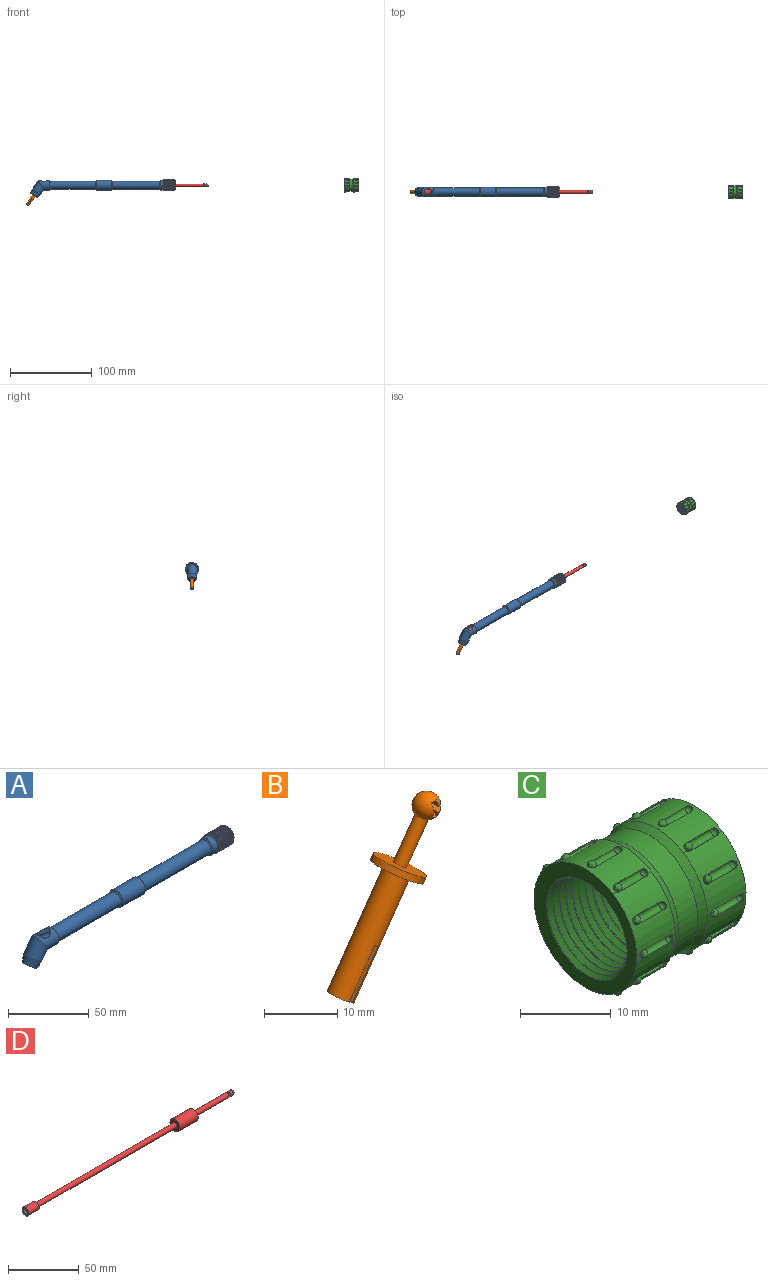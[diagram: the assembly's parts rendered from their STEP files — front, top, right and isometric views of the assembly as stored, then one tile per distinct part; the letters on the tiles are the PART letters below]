
ASSEMBLY  parts=4 mates=3
PART A: 38 faces, bbox 177.7x13x25.7 mm
  f0: bspline ~15.48x15.01mm, area 394.4mm2, adj f1,f2,f4,f5,f6,f7,f8,f9
  f1: bspline ~15.01x14.64mm, area 380.3mm2, adj f0,f3,f4,f5,f6,f7,f8,f9
  f2: cylinder r=6mm len=12mm, axis (-1,0,0), area 132.3mm2, adj f0,f17,f31,f37
  f3: cylinder r=6mm len=1.9mm, axis (-1,0,0), area 0mm2, adj f1,f4,f36
  f4: cylinder r=6mm len=12mm, axis (-1,0,0), area 1.9mm2, adj f0,f1,f3,f5
  f5: cylinder r=6mm len=12mm, axis (-1,0,0), area 1.9mm2, adj f0,f1,f4,f6
  f6: cylinder r=6mm len=12mm, axis (-1,0,0), area 1.9mm2, adj f0,f1,f5,f7
  f7: cylinder r=6mm len=12mm, axis (-1,0,0), area 1.9mm2, adj f0,f1,f6,f8
  f8: cylinder r=6mm len=12mm, axis (-1,0,0), area 1.9mm2, adj f0,f1,f7,f9
  f9: cylinder r=6mm len=12mm, axis (-1,0,0), area 1.9mm2, adj f0,f1,f8,f10
  f10: cylinder r=6mm len=12mm, axis (-1,0,0), area 1.9mm2, adj f0,f1,f9,f11
  f11: cylinder r=6mm len=12mm, axis (-1,0,0), area 1.9mm2, adj f0,f1,f10,f12
  f12: cylinder r=6mm len=12mm, axis (-1,0,0), area 1.9mm2, adj f0,f1,f11,f13
  f13: cylinder r=6mm len=12mm, axis (-1,0,0), area 1.9mm2, adj f0,f1,f12,f14
  f14: cylinder r=6mm len=12mm, axis (-1,0,0), area 1.9mm2, adj f0,f1,f13,f15
  f15: cylinder r=6mm len=12mm, axis (-1,0,0), area 1.9mm2, adj f0,f1,f14,f16
  f16: cylinder r=6mm len=12mm, axis (-1,0,0), area 1.9mm2, adj f0,f1,f15,f17
  f17: cylinder r=6mm len=12mm, axis (-1,0,0), area 1.9mm2, adj f0,f1,f2,f16
  f18: cylinder r=4mm len=21.07mm, axis (-0.57,0,-0.82), area 373.9mm2, adj f21,f28,f30
  f19: cylinder r=5mm len=54.5mm, axis (-1,0,0), area 1712.2mm2, adj f33,f34
  f20: cylinder r=5mm len=57.5mm, axis (-1,0,0), area 1806.4mm2, adj f31,f32
  f21: cylinder r=4mm len=147mm, axis (-1,0,0), area 3633mm2, adj f18,f23
  f22: plane 10x8.19mm, normal (-0.57,0,-0.82), area 66mm2, adj f29,f35
  f23: plane 10x10mm, normal (1,0,0), area 28.3mm2, adj f21,f24
  f24: cylinder r=5mm len=18mm, axis (-1,0,0), area 565.5mm2, adj f23,f25
  f25: plane 10.02x10.02mm, normal (1,0,0), area 0.3mm2, adj f24,f36
  f26: cylinder r=6mm len=19mm, axis (-1,0,0), area 716.3mm2, adj f32,f33
  f27: cylinder r=6mm len=17.63mm, axis (-0.57,0,-0.82), area 494.7mm2, adj f28,f35
  f28: cylinder r=6mm len=14.13mm, axis (-1,0,0), area 349.2mm2, adj f18,f27,f34
  f29: cylinder r=2mm len=6.39mm, axis (0.57,0,0.82), area 62.8mm2, adj f22,f30
  f30: plane 8x6.55mm, normal (0.57,0,0.82), area 37.7mm2, adj f18,f29
  f31: cone r=5mm half-angle=45deg, axis (1,0,0), area 48.9mm2, adj f2,f20
  f32: cone r=6mm half-angle=45deg, axis (-1,0,0), area 48.9mm2, adj f20,f26
  f33: cone r=6mm half-angle=45deg, axis (1,0,0), area 48.9mm2, adj f19,f26
  f34: cone r=7mm half-angle=45deg, axis (-1,0,0), area 48.9mm2, adj f19,f28
  f35: cone r=6mm half-angle=11.3deg, axis (0.57,0,0.82), area 176.2mm2, adj f22,f27
  f36: cone r=6mm half-angle=45deg, axis (-1,0,0), area 61.4mm2, adj f0,f1,f3,f25
  f37: plane 0.95x0.5mm, normal (0,0,1), area 0.2mm2, adj f0,f1,f2
PART B: 25 faces, bbox 20.3x8x26.9 mm
  f0: sphere r=2mm, area 35.4mm2, adj f2,f4,f6,f15,f16,f17,f18,f19
  f1: cylinder r=0.5mm len=1mm, axis (0,1,0), area 0.5mm2, adj f2,f15,f22
  f2: plane 3.74x1.94mm, normal (0,0,-1), area 4.5mm2, adj f0,f1,f15,f17,f21,f22
  f3: cylinder r=0.5mm len=1mm, axis (0,1,0), area 0.5mm2, adj f4,f18,f23
  f4: plane 3.74x1.94mm, normal (0,0,1), area 4.5mm2, adj f0,f3,f18,f19,f23,f24
  f5: plane 3.91x1.3mm, normal (-0.57,0,-0.82), area 4.6mm2, adj f10,f14
  f6: cylinder r=1mm len=7.1mm, axis (0.57,0,0.82), area 45.7mm2, adj f0,f7
  f7: plane 8x6.55mm, normal (0.57,0,0.82), area 47.1mm2, adj f6,f8
  f8: cylinder r=4mm len=8mm, axis (0.57,0,0.82), area 25.1mm2, adj f7,f9
  f9: plane 8x6.55mm, normal (-0.57,0,-0.82), area 37.7mm2, adj f8,f10
  f10: cylinder r=2mm len=17.86mm, axis (0.57,0,0.82), area 224.7mm2, adj f5,f9,f11,f12,f13,f14
  f11: plane 3.92x1.31mm, normal (-0.57,0,-0.82), area 4.7mm2, adj f10,f13
  f12: plane 4x0.67mm, normal (-0.57,0,-0.82), area 3.2mm2, adj f10,f13,f14
  f13: plane 7.04x4.93mm, normal (0.82,0,-0.57), area 33.7mm2, adj f10,f11,f12
  f14: plane 7.04x4.93mm, normal (-0.82,0,0.57), area 33.6mm2, adj f5,f10,f12
  f15: plane 1.41x1.41mm, normal (0,0.71,-0.71), area 1.3mm2, adj f0,f1,f2,f16,f17
  f16: plane 2.74x1.94mm, normal (1,0,0), area 2.9mm2, adj f0,f15,f18
  f17: plane 1.37x0.87mm, normal (-1,0,0), area 0.6mm2, adj f0,f2,f15
  f18: plane 1.41x1.41mm, normal (0,0.71,0.71), area 1.3mm2, adj f0,f3,f4,f16,f19
  f19: plane 1.37x0.87mm, normal (-1,0,0), area 0.6mm2, adj f0,f4,f18
  f20: plane 2.74x1.94mm, normal (1,0,0), area 2.9mm2, adj f0,f22,f23
  f21: plane 1.37x0.87mm, normal (-1,0,0), area 0.6mm2, adj f0,f2,f22
  f22: plane 1.41x1.41mm, normal (0,-0.71,-0.71), area 1.3mm2, adj f0,f1,f2,f20,f21
  f23: plane 1.41x1.41mm, normal (0,-0.71,0.71), area 1.3mm2, adj f0,f3,f4,f20,f24
  f24: plane 1.37x0.87mm, normal (-1,0,0), area 0.6mm2, adj f0,f4,f23
PART C: 85 faces, bbox 18.1x17.4x17.4 mm
  f0: sphere r=0.5mm, area 2.1mm2, adj f1,f3
  f1: cylinder r=0.5mm len=4mm, axis (1,0,0), area 6.2mm2, adj f0,f2,f3
  f2: sphere r=0.5mm, area 1.1mm2, adj f1,f3
  f3: cylinder r=8mm len=16mm, axis (1,0,0), area 247.6mm2, adj f0,f1,f2,f4,f5,f6,f7,f8
  f4: sphere r=0.5mm, area 1.1mm2, adj f3,f6
  f5: sphere r=0.5mm, area 2.1mm2, adj f3,f6
  f6: cylinder r=0.5mm len=4mm, axis (1,0,0), area 6.2mm2, adj f3,f4,f5
  f7: sphere r=0.5mm, area 1.1mm2, adj f3,f9
  f8: sphere r=0.5mm, area 2.1mm2, adj f3,f9
  f9: cylinder r=0.5mm len=4mm, axis (1,0,0), area 6.2mm2, adj f3,f7,f8
  f10: sphere r=0.5mm, area 1.1mm2, adj f3,f12
  f11: sphere r=0.5mm, area 2.1mm2, adj f3,f12
  f12: cylinder r=0.5mm len=4mm, axis (1,0,0), area 6.2mm2, adj f3,f10,f11
  f13: sphere r=0.5mm, area 1.1mm2, adj f3,f15
  f14: sphere r=0.5mm, area 2.1mm2, adj f3,f15
  f15: cylinder r=0.5mm len=4mm, axis (1,0,0), area 6.2mm2, adj f3,f13,f14
  f16: sphere r=0.5mm, area 1.1mm2, adj f3,f18
  f17: sphere r=0.5mm, area 2.1mm2, adj f3,f18
  f18: cylinder r=0.5mm len=4mm, axis (1,0,0), area 6.2mm2, adj f3,f16,f17
  f19: sphere r=0.5mm, area 1.1mm2, adj f3,f21
  f20: sphere r=0.5mm, area 2.1mm2, adj f3,f21
  f21: cylinder r=0.5mm len=4mm, axis (1,0,0), area 6.2mm2, adj f3,f19,f20
  f22: sphere r=0.5mm, area 1.1mm2, adj f3,f24
  f23: sphere r=0.5mm, area 2.1mm2, adj f3,f24
  f24: cylinder r=0.5mm len=4mm, axis (1,0,0), area 6.2mm2, adj f3,f22,f23
  f25: sphere r=0.5mm, area 1.1mm2, adj f3,f27
  f26: sphere r=0.5mm, area 2.1mm2, adj f3,f27
  f27: cylinder r=0.5mm len=4mm, axis (1,0,0), area 6.2mm2, adj f3,f25,f26
  f28: sphere r=0.5mm, area 1.1mm2, adj f3,f30
  f29: sphere r=0.5mm, area 2.1mm2, adj f3,f30
  f30: cylinder r=0.5mm len=4mm, axis (1,0,0), area 6.2mm2, adj f3,f28,f29
  f31: sphere r=0.5mm, area 1.1mm2, adj f3,f33
  f32: sphere r=0.5mm, area 2.1mm2, adj f3,f33
  f33: cylinder r=0.5mm len=4mm, axis (1,0,0), area 6.2mm2, adj f3,f31,f32
  f34: plane 16x16mm, normal (1,0,0), area 188.5mm2, adj f3,f35
  f35: cylinder r=2mm len=4mm, axis (1,0,0), area 25.1mm2, adj f34,f36
  f36: plane 12x12mm, normal (-1,0,0), area 100.5mm2, adj f35,f37
  f37: cylinder r=6mm len=15mm, axis (1,0,0), area -52mm2, adj f36,f38,f39,f79,f80
  f38: bspline ~15.5x15.01mm, area 409.7mm2, adj f37,f39,f79,f80
  f39: plane 16.45x16.45mm, normal (-1,0,0), area 78.4mm2, adj f37,f38,f40,f79
  f40: cylinder r=8mm len=16mm, axis (1,0,0), area 247.6mm2, adj f39,f41,f42,f43,f44,f45,f46,f47
  f41: sphere r=0.5mm, area 1.1mm2, adj f40,f43
  f42: sphere r=0.5mm, area 2.1mm2, adj f40,f43
  f43: cylinder r=0.5mm len=4mm, axis (1,0,0), area 6.2mm2, adj f40,f41,f42
  f44: sphere r=0.5mm, area 1.1mm2, adj f40,f46
  f45: sphere r=0.5mm, area 2.1mm2, adj f40,f46
  f46: cylinder r=0.5mm len=4mm, axis (1,0,0), area 6.2mm2, adj f40,f44,f45
  f47: sphere r=0.5mm, area 1.1mm2, adj f40,f49
  f48: sphere r=0.5mm, area 2.1mm2, adj f40,f49
  f49: cylinder r=0.5mm len=4mm, axis (1,0,0), area 6.2mm2, adj f40,f47,f48
  f50: sphere r=0.5mm, area 1.1mm2, adj f40,f52
  f51: sphere r=0.5mm, area 2.1mm2, adj f40,f52
  f52: cylinder r=0.5mm len=4mm, axis (1,0,0), area 6.2mm2, adj f40,f50,f51
  f53: sphere r=0.5mm, area 1.1mm2, adj f40,f55
  f54: sphere r=0.5mm, area 2.1mm2, adj f40,f55
  f55: cylinder r=0.5mm len=4mm, axis (1,0,0), area 6.2mm2, adj f40,f53,f54
  f56: sphere r=0.5mm, area 1.1mm2, adj f40,f58
  f57: sphere r=0.5mm, area 2.1mm2, adj f40,f58
  f58: cylinder r=0.5mm len=4mm, axis (1,0,0), area 6.2mm2, adj f40,f56,f57
  f59: sphere r=0.5mm, area 1.1mm2, adj f40,f61
  f60: sphere r=0.5mm, area 2.1mm2, adj f40,f61
  f61: cylinder r=0.5mm len=4mm, axis (1,0,0), area 6.2mm2, adj f40,f59,f60
  f62: sphere r=0.5mm, area 1.1mm2, adj f40,f64
  f63: sphere r=0.5mm, area 2.1mm2, adj f40,f64
  f64: cylinder r=0.5mm len=4mm, axis (1,0,0), area 6.2mm2, adj f40,f62,f63
  f65: sphere r=0.5mm, area 1.1mm2, adj f40,f67
  f66: sphere r=0.5mm, area 2.1mm2, adj f40,f67
  f67: cylinder r=0.5mm len=4mm, axis (1,0,0), area 6.2mm2, adj f40,f65,f66
  f68: sphere r=0.5mm, area 1.1mm2, adj f40,f70
  f69: sphere r=0.5mm, area 2.1mm2, adj f40,f70
  f70: cylinder r=0.5mm len=4mm, axis (1,0,0), area 6.2mm2, adj f40,f68,f69
  f71: sphere r=0.5mm, area 1.1mm2, adj f40,f73
  f72: sphere r=0.5mm, area 2.1mm2, adj f40,f73
  f73: cylinder r=0.5mm len=4mm, axis (1,0,0), area 6.2mm2, adj f40,f71,f72
  f74: cone r=8mm half-angle=26.6deg, axis (-1,0,0), area 54.4mm2, adj f40,f75
  f75: cylinder r=7.5mm len=15mm, axis (1,0,0), area 141.4mm2, adj f74,f82
  f76: sphere r=0.5mm, area 1.1mm2, adj f40,f78
  f77: sphere r=0.5mm, area 2.1mm2, adj f40,f78
  f78: cylinder r=0.5mm len=4mm, axis (1,0,0), area 6.2mm2, adj f40,f76,f77
  f79: bspline ~15.16x15.01mm, area 396.2mm2, adj f37,f38,f39,f80
  f80: plane 0.99x0.5mm, normal (0,0,-1), area 0.2mm2, adj f37,f38,f79
  f81: sphere r=0.5mm, area 1.1mm2, adj f3,f84
  f82: cone r=7.5mm half-angle=26.6deg, axis (1,0,0), area 54.4mm2, adj f3,f75
  f83: sphere r=0.5mm, area 2.1mm2, adj f3,f84
  f84: cylinder r=0.5mm len=4mm, axis (1,0,0), area 6.2mm2, adj f3,f81,f83
PART D: 14 faces, bbox 207x10x10 mm
  f0: cylinder r=2mm len=4mm, axis (1,0,0), area 24.3mm2, adj f1,f12,f13
  f1: sphere r=2mm, area 24.3mm2, adj f0,f13
  f2: sphere r=2mm, area 25.1mm2, adj f3
  f3: cylinder r=2mm len=4mm, axis (1,0,0), area 31.8mm2, adj f2,f4
  f4: torus R=2.12mm, axis (1,0,0), area 21.1mm2, adj f3,f5
  f5: cylinder r=2mm len=33.99mm, axis (1,0,0), area 427.1mm2, adj f4,f6
  f6: plane 10x10mm, normal (1,0,0), area 66mm2, adj f5,f7
  f7: cylinder r=5mm len=18mm, axis (1,0,0), area 565.5mm2, adj f6,f8
  f8: plane 10x10mm, normal (-1,0,0), area 66mm2, adj f7,f9
  f9: cylinder r=2mm len=139mm, axis (1,0,0), area 1746.7mm2, adj f8,f10
  f10: plane 7x7mm, normal (1,0,0), area 25.9mm2, adj f9,f11
  f11: cylinder r=3.5mm len=10mm, axis (1,0,0), area 219.9mm2, adj f10,f12
  f12: plane 7x7mm, normal (-1,0,0), area 25.9mm2, adj f0,f11
  f13: cylinder r=0.5mm len=4mm, axis (0,1,0), area 12.3mm2, adj f0,f1
PLACE A at identity fixed
PLACE B t=(-165,0,0)mm
PLACE C rot(axis=(1,0,0),129.2deg) t=(222.6,0,0)mm
PLACE D t=(-18,0,0)mm
MATE slider D.f0 <-> A.f2  axis (-1,0,0) through (-18,0,0)mm
MATE slider B.f6 <-> A.f18  axis (-0.57,0,-0.82) through (-170.74,0,-8.19)mm
MATE cylindrical C.f3 <-> A.f24  axis (-1,0,0) through (205.6,0,0)mm
